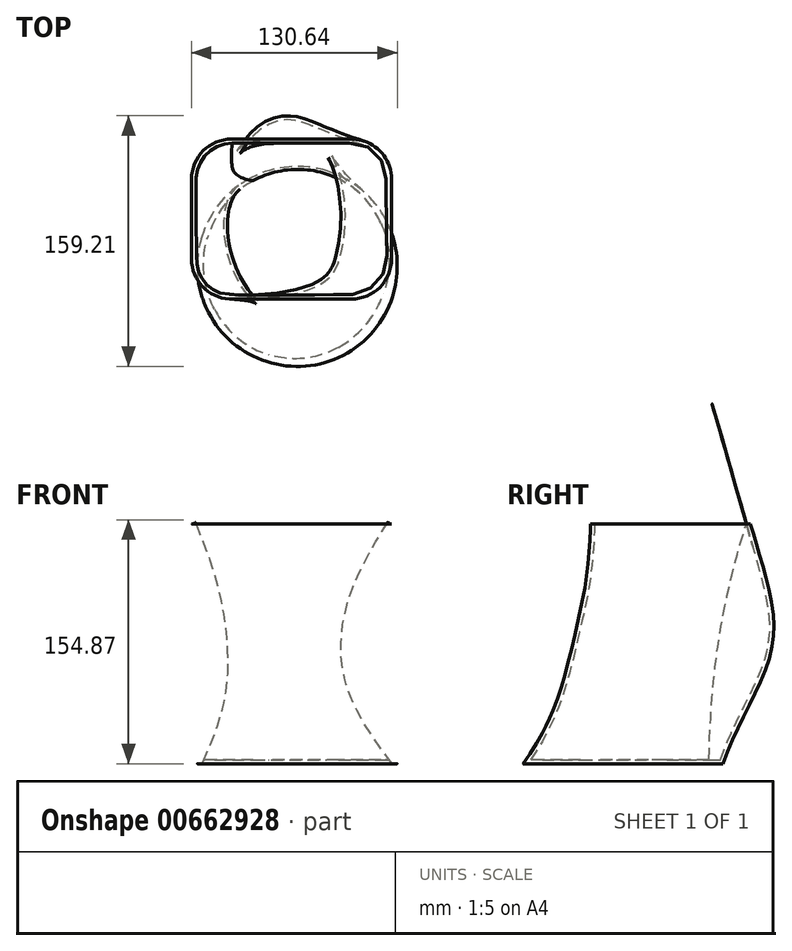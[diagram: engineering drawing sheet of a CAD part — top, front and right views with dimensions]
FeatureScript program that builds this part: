
annotation { "Feature Type Name" : "Feature", "Feature Type Description" : "" }
export const myFeature = defineFeature(function(context is Context, id is Id, definition is map)
    precondition{}
    {
        {
            var Q0;
            Q0=qCreatedBy(makeId("Top.planeOp"),FACE);
            cPlane(context, id + "F0", {"entities" : qUnion([Q0]), "cplaneType" : CPlaneType.OFFSET, "offset" : 76.2 * mm, "width" : 152.4 * mm, "height" : 152.4 * mm});
        }
        {
            var Q0;
            Q0=qCreatedBy(id+"F0.planeOp",FACE);
            cPlane(context, id + "F1", {"entities" : qUnion([Q0]), "cplaneType" : CPlaneType.OFFSET, "offset" : 76.2 * mm, "width" : 152.4 * mm, "height" : 152.4 * mm});
        }
        {
            var Q0;
            Q0=qCreatedBy(makeId("Top.planeOp"),FACE);
            var sketch = newSketch(context, id + "F2", { "sketchPlane" : qUnion([Q0])});
            skCircle(sketch, "E0", {"center": v(-10.25, -2.84) * mm, "radius": 63.5 * mm});
            skSolve(sketch);
        }
        {
            var Q0;
            Q0=qCreatedBy(id+"F0.planeOp",FACE);
            var sketch = newSketch(context, id + "F3", { "sketchPlane" : qUnion([Q0])});
            skEllipse(sketch, "E1", {"center": v(-18.74, 28.58) * mm, "majorRadius": 63.5 * mm, "minorRadius": 38.76 * mm, "majorAxis": v(0, -1)});
            skSolve(sketch);
        }
        {
            var Q0;
            Q0=qCreatedBy(id+"F1.planeOp",FACE);
            var sketch = newSketch(context, id + "F4", { "sketchPlane" : qUnion([Q0])});
            skLineSegment(sketch, "E2.bottom", {"start": v(-52, 78.04) * mm, "end": v(24.2, 78.04) * mm});
            skLineSegment(sketch, "E2.top", {"start": v(-52, -23.56) * mm, "end": v(24.2, -23.56) * mm});
            skLineSegment(sketch, "E2.left", {"start": v(-77.4, 52.64) * mm, "end": v(-77.4, 1.84) * mm});
            skLineSegment(sketch, "E2.right", {"start": v(49.6, 52.64) * mm, "end": v(49.6, 1.84) * mm});
            skPoint(sketch, "E3.visualSharp", {"position": v(-77.4, 78.04) * mm});
            skArc(sketch, "E3.filletArc", {"start": v(-52, 78.04) * mm, "mid": v(-69.95, 70.6) * mm, "end": v(-77.4, 52.64) * mm});
            skPoint(sketch, "E4.visualSharp", {"position": v(-77.4, -23.56) * mm});
            skArc(sketch, "E4.filletArc", {"start": v(-77.4, 1.84) * mm, "mid": v(-69.95, -16.12) * mm, "end": v(-52, -23.56) * mm});
            skPoint(sketch, "E5.visualSharp", {"position": v(49.6, -23.56) * mm});
            skArc(sketch, "E5.filletArc", {"start": v(24.2, -23.56) * mm, "mid": v(42.17, -16.12) * mm, "end": v(49.6, 1.84) * mm});
            skPoint(sketch, "E6.visualSharp", {"position": v(49.6, 78.04) * mm});
            skArc(sketch, "E6.filletArc", {"start": v(49.6, 52.64) * mm, "mid": v(42.17, 70.6) * mm, "end": v(24.2, 78.04) * mm});
            skSolve(sketch);
        }
        {
            var Q0;
            Q0=makeQuery(id+"F2.imprint","IMPRINT",FACE,{"disambiguationData":[TD([[makeQuery(id+"F2.imprint","IMPRINT",EDGE,{"derivedFrom":sQuery(id+"F2.wireOp",EDGE,"E0")}),1.0]])]});
            var Q1;
            Q1=makeQuery(id+"F3.imprint","IMPRINT",FACE,{"disambiguationData":[TD([[makeQuery(id+"F3.imprint","IMPRINT",EDGE,{"derivedFrom":sQuery(id+"F3.wireOp",EDGE,"E1")}),1.0]])]});
            var Q2;
            Q2=makeQuery(id+"F4.imprint","IMPRINT",FACE,{"disambiguationData":[TD([[makeQuery(id+"F4.imprint","IMPRINT",EDGE,{"derivedFrom":sQuery(id+"F4.wireOp",EDGE,"E2.bottom")}),-1.0]])]});
            loft(context, id + "F5", {"sheetProfilesArray" : [{ "sheetProfileEntities" : qUnion([Q0]) }, { "sheetProfileEntities" : qUnion([Q1]) }, { "sheetProfileEntities" : qUnion([Q2]) }]});
        }
        {
            var Q0;
            Q0=makeQuery(id+"F5.opLoft","CAP_FACE",FACE,{"disambiguationData":[OSD([makeQuery(id+"F4.imprint","IMPRINT",FACE,{"disambiguationData":[TD([[makeQuery(id+"F4.imprint","IMPRINT",EDGE,{"derivedFrom":sQuery(id+"F4.wireOp",EDGE,"E2.bottom")}),-1.0]])]})])],"isStart":true});
            shell(context, id + "F6", {"entities" : qUnion([Q0]), "thickness" : 2.54 * mm});
        }
    });
